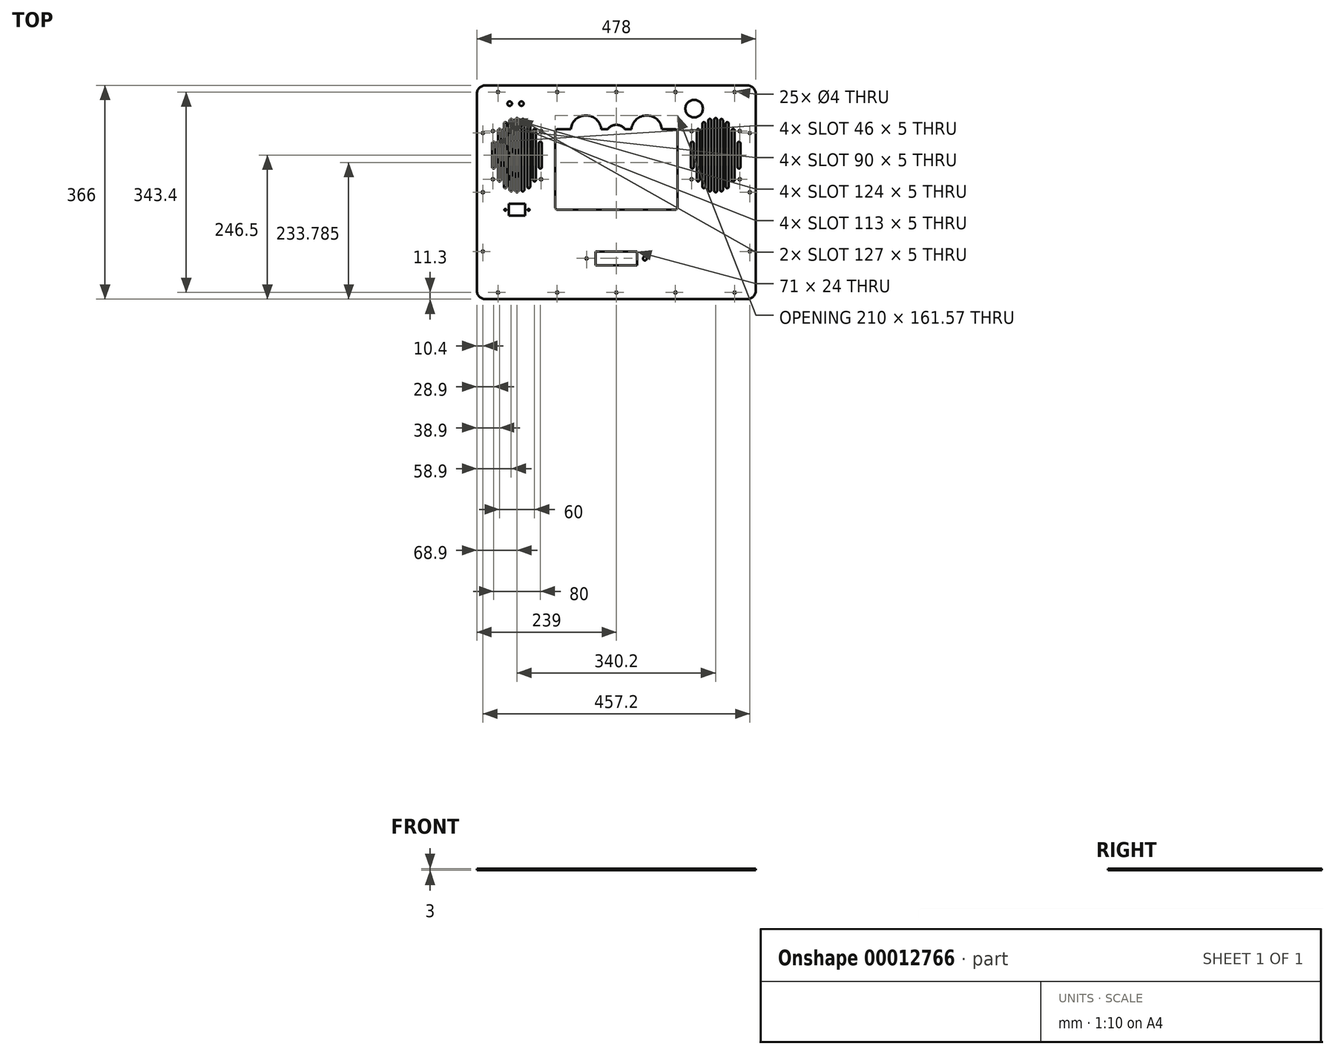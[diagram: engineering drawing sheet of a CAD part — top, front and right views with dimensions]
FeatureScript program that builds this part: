
annotation { "Feature Type Name" : "Feature", "Feature Type Description" : "" }
export const myFeature = defineFeature(function(context is Context, id is Id, definition is map)
    precondition{}
    {
        {
            var Q0;
            Q0=qCreatedBy(makeId("Top.planeOp"),FACE);
            var sketch = newSketch(context, id + "F0", { "sketchPlane" : qUnion([Q0])});
            skLineSegment(sketch, "E0.rect.bottom", {"start": v(-228.6, 171.7) * mm, "end": v(228.6, 171.7) * mm, "construction": true});
            skLineSegment(sketch, "E0.rect.top", {"start": v(-228.6, -171.7) * mm, "end": v(228.6, -171.7) * mm});
            skLineSegment(sketch, "E0.rect.left", {"start": v(-228.6, 171.7) * mm, "end": v(-228.6, -171.7) * mm, "construction": true});
            skLineSegment(sketch, "E0.rect.right", {"start": v(228.6, 171.7) * mm, "end": v(228.6, -171.7) * mm, "construction": true});
            skPoint(sketch, "E1", {"position": v(0, 171.7) * mm});
            skPoint(sketch, "E2", {"position": v(-228.6, 0) * mm});
            skCircle(sketch, "E3", {"center": v(0, 171.7) * mm, "radius": 2 * mm});
            skCircle(sketch, "E4", {"center": v(0, -171.7) * mm, "radius": 2 * mm});
            skCircle(sketch, "E5", {"center": v(-228.6, 0) * mm, "radius": 2 * mm});
            skLineSegment(sketch, "E6.rect.bottom", {"start": v(-239, 183) * mm, "end": v(239, 183) * mm});
            skLineSegment(sketch, "E6.rect.top", {"start": v(-239, -183) * mm, "end": v(239, -183) * mm});
            skLineSegment(sketch, "E6.rect.left", {"start": v(-239, 183) * mm, "end": v(-239, -183) * mm});
            skLineSegment(sketch, "E6.rect.right", {"start": v(239, 183) * mm, "end": v(239, -183) * mm});
            skLineSegment(sketch, "E7.rect.bottom", {"start": v(-222.5, 165) * mm, "end": v(222.5, 165) * mm, "construction": true});
            skLineSegment(sketch, "E7.rect.top", {"start": v(-222.5, -165) * mm, "end": v(222.5, -165) * mm});
            skLineSegment(sketch, "E7.rect.left", {"start": v(-222.5, 165) * mm, "end": v(-222.5, -165) * mm, "construction": true});
            skLineSegment(sketch, "E7.rect.right", {"start": v(222.5, 165) * mm, "end": v(222.5, -165) * mm, "construction": true});
            skCircle(sketch, "E8", {"center": v(228.6, 0) * mm, "radius": 2 * mm});
            skLineSegment(sketch, "E9.bottom", {"start": v(-192.6, 120) * mm, "end": v(-187.6, 120) * mm});
            skLineSegment(sketch, "E9.top", {"start": v(-192.6, 7) * mm, "end": v(-187.6, 7) * mm});
            skLineSegment(sketch, "E9.left", {"start": v(-192.6, 120) * mm, "end": v(-192.6, 7) * mm});
            skLineSegment(sketch, "E9.right", {"start": v(-187.6, 120) * mm, "end": v(-187.6, 7) * mm});
            skLineSegment(sketch, "E10.bottom", {"start": v(-105, 108) * mm, "end": v(105, 108) * mm});
            skLineSegment(sketch, "E10.left", {"start": v(-105, 108) * mm, "end": v(-105, -30) * mm});
            skLineSegment(sketch, "E10.right", {"start": v(105, 108) * mm, "end": v(105, -30) * mm});
            skCircle(sketch, "E11", {"center": v(-228.6, -101.3) * mm, "radius": 2 * mm});
            skLineSegment(sketch, "E12.0", {"start": v(-228.6, -171.7) * mm, "end": v(228.6, -171.7) * mm, "construction": true});
            skLineSegment(sketch, "E13", {"start": v(-228.6, 0) * mm, "end": v(228.6, 0) * mm, "construction": true});
            skLineSegment(sketch, "E14.0", {"start": v(-228.6, -101.3) * mm, "end": v(228.6, -101.3) * mm});
            skCircle(sketch, "E15", {"center": v(228.6, -101.3) * mm, "radius": 2 * mm});
            skLineSegment(sketch, "E16.0", {"start": v(-228.6, 101.3) * mm, "end": v(228.6, 101.3) * mm, "construction": true});
            skCircle(sketch, "E17", {"center": v(228.6, 101.3) * mm, "radius": 2 * mm});
            skCircle(sketch, "E18", {"center": v(-228.6, 101.3) * mm, "radius": 2 * mm});
            skLineSegment(sketch, "E19", {"start": v(0, 171.7) * mm, "end": v(0, -171.7) * mm, "construction": true});
            skLineSegment(sketch, "E20.0", {"start": v(-101.3, 171.7) * mm, "end": v(-101.3, -171.7) * mm, "construction": true});
            skCircle(sketch, "E21", {"center": v(-101.3, -171.7) * mm, "radius": 2 * mm});
            skCircle(sketch, "E22", {"center": v(-101.3, 171.7) * mm, "radius": 2 * mm});
            skLineSegment(sketch, "E23.0", {"start": v(-202.6, 171.7) * mm, "end": v(-202.6, -171.7) * mm, "construction": true});
            skCircle(sketch, "E24", {"center": v(-202.6, -171.7) * mm, "radius": 2 * mm});
            skCircle(sketch, "E25", {"center": v(-202.6, 171.7) * mm, "radius": 2 * mm});
            skLineSegment(sketch, "E26.0", {"start": v(101.3, 171.7) * mm, "end": v(101.3, -171.7) * mm, "construction": true});
            skLineSegment(sketch, "E27.0", {"start": v(202.6, 171.7) * mm, "end": v(202.6, -171.7) * mm, "construction": true});
            skCircle(sketch, "E28", {"center": v(101.3, -171.7) * mm, "radius": 2 * mm});
            skCircle(sketch, "E29", {"center": v(202.6, -171.7) * mm, "radius": 2 * mm});
            skCircle(sketch, "E30", {"center": v(101.3, 171.7) * mm, "radius": 2 * mm});
            skCircle(sketch, "E31", {"center": v(202.6, 171.7) * mm, "radius": 2 * mm});
            skPoint(sketch, "E32", {"position": v(-192.6, 63.5) * mm});
            skPoint(sketch, "E33", {"position": v(-190.28, 120) * mm});
            skLineSegment(sketch, "E34", {"start": v(-187.6, 63.5) * mm, "end": v(-192.6, 63.5) * mm, "construction": true});
            skPoint(sketch, "E35", {"position": v(-190.1, 63.5) * mm});
            skLineSegment(sketch, "E36.bottom", {"start": v(-212.6, 86.5) * mm, "end": v(-207.6, 86.5) * mm});
            skLineSegment(sketch, "E36.top", {"start": v(-212.6, 40.5) * mm, "end": v(-207.6, 40.5) * mm});
            skLineSegment(sketch, "E36.left", {"start": v(-212.6, 86.5) * mm, "end": v(-212.6, 40.5) * mm});
            skLineSegment(sketch, "E36.right", {"start": v(-207.6, 86.5) * mm, "end": v(-207.6, 40.5) * mm});
            skPoint(sketch, "E37", {"position": v(-212.6, 63.5) * mm});
            skLineSegment(sketch, "E38.bottom", {"start": v(-202.6, 108.5) * mm, "end": v(-197.6, 108.5) * mm});
            skLineSegment(sketch, "E38.top", {"start": v(-202.6, 18.5) * mm, "end": v(-197.6, 18.5) * mm});
            skLineSegment(sketch, "E38.left", {"start": v(-202.6, 108.5) * mm, "end": v(-202.6, 18.5) * mm});
            skLineSegment(sketch, "E38.right", {"start": v(-197.6, 108.5) * mm, "end": v(-197.6, 18.5) * mm});
            skPoint(sketch, "E39", {"position": v(-202.6, 63.5) * mm});
            skLineSegment(sketch, "E40.0", {"start": v(-212.6, 171.7) * mm, "end": v(-212.6, -171.7) * mm, "construction": true});
            skLineSegment(sketch, "E41.0", {"start": v(-192.6, 171.7) * mm, "end": v(-192.6, -171.7) * mm, "construction": true});
            skLineSegment(sketch, "E42.bottom", {"start": v(-182.6, 125.5) * mm, "end": v(-177.6, 125.5) * mm});
            skLineSegment(sketch, "E42.top", {"start": v(-182.6, 1.5) * mm, "end": v(-177.6, 1.5) * mm});
            skLineSegment(sketch, "E42.left", {"start": v(-182.6, 125.5) * mm, "end": v(-182.6, 1.5) * mm});
            skLineSegment(sketch, "E42.right", {"start": v(-177.6, 125.5) * mm, "end": v(-177.6, 1.5) * mm});
            skLineSegment(sketch, "E43.0", {"start": v(-182.6, 171.7) * mm, "end": v(-182.6, -171.7) * mm, "construction": true});
            skPoint(sketch, "E44", {"position": v(-182.6, 63.5) * mm});
            skLineSegment(sketch, "E45.bottom", {"start": v(-172.6, 127) * mm, "end": v(-167.6, 127) * mm});
            skLineSegment(sketch, "E45.top", {"start": v(-172.6, 0) * mm, "end": v(-167.6, 0) * mm});
            skLineSegment(sketch, "E45.left", {"start": v(-172.6, 127) * mm, "end": v(-172.6, 0) * mm});
            skLineSegment(sketch, "E45.right", {"start": v(-167.6, 127) * mm, "end": v(-167.6, 0) * mm});
            skPoint(sketch, "E46", {"position": v(-172.6, 63.5) * mm});
            skLineSegment(sketch, "E47.0", {"start": v(-172.6, 171.7) * mm, "end": v(-172.6, -171.7) * mm, "construction": true});
            skLineSegment(sketch, "E48.bottom", {"start": v(-162.6, 125.5) * mm, "end": v(-157.6, 125.5) * mm});
            skLineSegment(sketch, "E48.top", {"start": v(-162.6, 1.5) * mm, "end": v(-157.6, 1.5) * mm});
            skLineSegment(sketch, "E48.left", {"start": v(-162.6, 125.5) * mm, "end": v(-162.6, 1.5) * mm});
            skLineSegment(sketch, "E48.right", {"start": v(-157.6, 125.5) * mm, "end": v(-157.6, 1.5) * mm});
            skPoint(sketch, "E49", {"position": v(-162.6, 63.5) * mm});
            skLineSegment(sketch, "E50.0", {"start": v(-162.6, 171.7) * mm, "end": v(-162.6, -171.7) * mm, "construction": true});
            skLineSegment(sketch, "E51.bottom", {"start": v(-152.6, 120) * mm, "end": v(-147.6, 120) * mm});
            skLineSegment(sketch, "E51.top", {"start": v(-152.6, 7) * mm, "end": v(-147.6, 7) * mm});
            skLineSegment(sketch, "E51.left", {"start": v(-152.6, 120) * mm, "end": v(-152.6, 7) * mm});
            skLineSegment(sketch, "E51.right", {"start": v(-147.6, 120) * mm, "end": v(-147.6, 7) * mm});
            skPoint(sketch, "E52", {"position": v(-152.6, 63.5) * mm});
            skLineSegment(sketch, "E53.bottom", {"start": v(-142.6, 108.5) * mm, "end": v(-137.6, 108.5) * mm});
            skLineSegment(sketch, "E53.top", {"start": v(-142.6, 18.5) * mm, "end": v(-137.6, 18.5) * mm});
            skLineSegment(sketch, "E53.left", {"start": v(-142.6, 108.5) * mm, "end": v(-142.6, 18.5) * mm});
            skLineSegment(sketch, "E53.right", {"start": v(-137.6, 108.5) * mm, "end": v(-137.6, 18.5) * mm});
            skPoint(sketch, "E54", {"position": v(-142.6, 63.5) * mm});
            skLineSegment(sketch, "E55.0", {"start": v(-152.6, 171.7) * mm, "end": v(-152.6, -171.7) * mm, "construction": true});
            skLineSegment(sketch, "E56.0", {"start": v(-142.6, 171.7) * mm, "end": v(-142.6, -171.7) * mm, "construction": true});
            skLineSegment(sketch, "E57.bottom", {"start": v(-132.6, 86.5) * mm, "end": v(-127.6, 86.5) * mm});
            skLineSegment(sketch, "E57.top", {"start": v(-132.6, 40.5) * mm, "end": v(-127.6, 40.5) * mm});
            skLineSegment(sketch, "E57.left", {"start": v(-132.6, 86.5) * mm, "end": v(-132.6, 40.5) * mm});
            skLineSegment(sketch, "E57.right", {"start": v(-127.6, 86.5) * mm, "end": v(-127.6, 40.5) * mm});
            skPoint(sketch, "E58", {"position": v(-132.6, 63.5) * mm});
            skLineSegment(sketch, "E59.0", {"start": v(-132.6, 171.7) * mm, "end": v(-132.6, -171.7) * mm, "construction": true});
            skLineSegment(sketch, "E60", {"start": v(-172.6, 63.5) * mm, "end": v(-167.6, 63.5) * mm});
            skPoint(sketch, "E61", {"position": v(-170.1, 63.5) * mm});
            skLineSegment(sketch, "E62.rect.bottom", {"start": v(-128.85, 104.75) * mm, "end": v(-211.35, 104.75) * mm, "construction": true});
            skLineSegment(sketch, "E62.rect.top", {"start": v(-128.85, 22.25) * mm, "end": v(-211.35, 22.25) * mm, "construction": true});
            skLineSegment(sketch, "E62.rect.left", {"start": v(-128.85, 104.75) * mm, "end": v(-128.85, 22.25) * mm, "construction": true});
            skLineSegment(sketch, "E62.rect.right", {"start": v(-211.35, 104.75) * mm, "end": v(-211.35, 22.25) * mm, "construction": true});
            skCircle(sketch, "E63", {"center": v(-128.85, 104.75) * mm, "radius": 2 * mm});
            skCircle(sketch, "E64", {"center": v(-128.85, 22.25) * mm, "radius": 2 * mm});
            skCircle(sketch, "E65", {"center": v(-211.35, 22.25) * mm, "radius": 2 * mm});
            skCircle(sketch, "E66", {"center": v(-211.35, 104.75) * mm, "radius": 2 * mm});
            skLineSegment(sketch, "E67.0.MirrorCS", {"start": v(192.6, 120) * mm, "end": v(187.6, 120) * mm});
            skLineSegment(sketch, "E67.1.MirrorCS", {"start": v(152.6, 7) * mm, "end": v(147.6, 7) * mm});
            skLineSegment(sketch, "E67.2.MirrorCS", {"start": v(182.6, 125.5) * mm, "end": v(177.6, 125.5) * mm});
            skLineSegment(sketch, "E67.3.MirrorCS", {"start": v(192.6, 7) * mm, "end": v(187.6, 7) * mm});
            skLineSegment(sketch, "E67.4.MirrorCS", {"start": v(152.6, 120) * mm, "end": v(147.6, 120) * mm});
            skLineSegment(sketch, "E67.5.MirrorCS", {"start": v(162.6, 1.5) * mm, "end": v(157.6, 1.5) * mm});
            skLineSegment(sketch, "E67.6.MirrorCS", {"start": v(132.6, 86.5) * mm, "end": v(127.6, 86.5) * mm});
            skLineSegment(sketch, "E67.7.MirrorCS", {"start": v(202.6, 108.5) * mm, "end": v(197.6, 108.5) * mm});
            skLineSegment(sketch, "E67.8.MirrorCS", {"start": v(172.6, 63.5) * mm, "end": v(167.6, 63.5) * mm});
            skLineSegment(sketch, "E67.9.MirrorCS", {"start": v(172.6, 0) * mm, "end": v(167.6, 0) * mm});
            skLineSegment(sketch, "E67.10.MirrorCS", {"start": v(212.6, 40.5) * mm, "end": v(207.6, 40.5) * mm});
            skLineSegment(sketch, "E67.11.MirrorCS", {"start": v(142.6, 108.5) * mm, "end": v(137.6, 108.5) * mm});
            skCircle(sketch, "E67.12.MirrorC", {"center": v(211.35, 22.25) * mm, "radius": 2 * mm});
            skLineSegment(sketch, "E67.13.MirrorCS", {"start": v(172.6, 127) * mm, "end": v(167.6, 127) * mm});
            skLineSegment(sketch, "E67.14.MirrorCS", {"start": v(212.6, 86.5) * mm, "end": v(207.6, 86.5) * mm});
            skCircle(sketch, "E67.15.MirrorC", {"center": v(128.85, 104.75) * mm, "radius": 2 * mm});
            skCircle(sketch, "E67.16.MirrorC", {"center": v(128.85, 22.25) * mm, "radius": 2 * mm});
            skLineSegment(sketch, "E67.17.MirrorCS", {"start": v(182.6, 1.5) * mm, "end": v(177.6, 1.5) * mm});
            skLineSegment(sketch, "E67.18.MirrorCS", {"start": v(202.6, 18.5) * mm, "end": v(197.6, 18.5) * mm});
            skLineSegment(sketch, "E67.19.MirrorCS", {"start": v(132.6, 40.5) * mm, "end": v(127.6, 40.5) * mm});
            skLineSegment(sketch, "E67.20.MirrorCS", {"start": v(162.6, 125.5) * mm, "end": v(157.6, 125.5) * mm});
            skCircle(sketch, "E67.21.MirrorC", {"center": v(211.35, 104.75) * mm, "radius": 2 * mm});
            skLineSegment(sketch, "E67.22.MirrorCS", {"start": v(187.6, 63.5) * mm, "end": v(192.6, 63.5) * mm, "construction": true});
            skPoint(sketch, "E67.23.MirrorP", {"position": v(170.1, 63.5) * mm});
            skPoint(sketch, "E67.24.MirrorP", {"position": v(172.6, 63.5) * mm});
            skLineSegment(sketch, "E67.25.MirrorCS", {"start": v(142.6, 18.5) * mm, "end": v(137.6, 18.5) * mm});
            skLineSegment(sketch, "E67.26.MirrorCS", {"start": v(172.6, 127) * mm, "end": v(172.6, 0) * mm});
            skLineSegment(sketch, "E67.27.MirrorCS", {"start": v(212.6, 86.5) * mm, "end": v(212.6, 40.5) * mm});
            skPoint(sketch, "E67.28.MirrorP", {"position": v(190.1, 63.5) * mm});
            skLineSegment(sketch, "E67.29.MirrorCS", {"start": v(128.85, 22.25) * mm, "end": v(211.35, 22.25) * mm, "construction": true});
            skPoint(sketch, "E67.30.MirrorP", {"position": v(212.6, 63.5) * mm});
            skLineSegment(sketch, "E67.31.MirrorCS", {"start": v(207.6, 86.5) * mm, "end": v(207.6, 40.5) * mm});
            skLineSegment(sketch, "E67.32.MirrorCS", {"start": v(167.6, 127) * mm, "end": v(167.6, 0) * mm});
            skPoint(sketch, "E67.33.MirrorP", {"position": v(202.6, 63.5) * mm});
            skLineSegment(sketch, "E67.34.MirrorCS", {"start": v(128.85, 104.75) * mm, "end": v(211.35, 104.75) * mm, "construction": true});
            skPoint(sketch, "E67.35.MirrorP", {"position": v(132.6, 63.5) * mm});
            skLineSegment(sketch, "E67.36.MirrorCS", {"start": v(202.6, 108.5) * mm, "end": v(202.6, 18.5) * mm});
            skLineSegment(sketch, "E67.37.MirrorCS", {"start": v(132.6, 86.5) * mm, "end": v(132.6, 40.5) * mm});
            skLineSegment(sketch, "E67.38.MirrorCS", {"start": v(192.6, 120) * mm, "end": v(192.6, 7) * mm});
            skPoint(sketch, "E67.39.MirrorP", {"position": v(162.6, 63.5) * mm});
            skLineSegment(sketch, "E67.40.MirrorCS", {"start": v(162.6, 125.5) * mm, "end": v(162.6, 1.5) * mm});
            skLineSegment(sketch, "E67.41.MirrorCS", {"start": v(127.6, 86.5) * mm, "end": v(127.6, 40.5) * mm});
            skLineSegment(sketch, "E67.42.MirrorCS", {"start": v(137.6, 108.5) * mm, "end": v(137.6, 18.5) * mm});
            skLineSegment(sketch, "E67.43.MirrorCS", {"start": v(197.6, 108.5) * mm, "end": v(197.6, 18.5) * mm});
            skPoint(sketch, "E67.44.MirrorP", {"position": v(142.6, 63.5) * mm});
            skLineSegment(sketch, "E67.45.MirrorCS", {"start": v(177.6, 125.5) * mm, "end": v(177.6, 1.5) * mm});
            skPoint(sketch, "E67.46.MirrorP", {"position": v(190.28, 120) * mm});
            skPoint(sketch, "E67.47.MirrorP", {"position": v(152.6, 63.5) * mm});
            skLineSegment(sketch, "E67.48.MirrorCS", {"start": v(142.6, 108.5) * mm, "end": v(142.6, 18.5) * mm});
            skPoint(sketch, "E67.49.MirrorP", {"position": v(192.6, 63.5) * mm});
            skPoint(sketch, "E67.50.MirrorP", {"position": v(170.1, 63.5) * mm});
            skLineSegment(sketch, "E67.51.MirrorCS", {"start": v(157.6, 125.5) * mm, "end": v(157.6, 1.5) * mm});
            skPoint(sketch, "E67.52.MirrorP", {"position": v(182.6, 63.5) * mm});
            skLineSegment(sketch, "E67.53.MirrorCS", {"start": v(128.85, 104.75) * mm, "end": v(128.85, 22.25) * mm, "construction": true});
            skLineSegment(sketch, "E67.54.MirrorCS", {"start": v(152.6, 120) * mm, "end": v(152.6, 7) * mm});
            skLineSegment(sketch, "E67.55.MirrorCS", {"start": v(187.6, 120) * mm, "end": v(187.6, 7) * mm});
            skLineSegment(sketch, "E67.56.MirrorCS", {"start": v(211.35, 104.75) * mm, "end": v(211.35, 22.25) * mm, "construction": true});
            skLineSegment(sketch, "E67.57.MirrorCS", {"start": v(147.6, 120) * mm, "end": v(147.6, 7) * mm});
            skLineSegment(sketch, "E67.58.MirrorCS", {"start": v(182.6, 125.5) * mm, "end": v(182.6, 1.5) * mm});
            skCircle(sketch, "E68", {"center": v(133.3, 143.2) * mm, "radius": 15 * mm});
            skLineSegment(sketch, "E69.bottom", {"start": v(-35.5, -101.3) * mm, "end": v(35.5, -101.3) * mm});
            skLineSegment(sketch, "E69.top", {"start": v(-35.5, -125.3) * mm, "end": v(35.5, -125.3) * mm});
            skLineSegment(sketch, "E69.left", {"start": v(-35.5, -101.3) * mm, "end": v(-35.5, -125.3) * mm});
            skLineSegment(sketch, "E69.right", {"start": v(35.5, -101.3) * mm, "end": v(35.5, -125.3) * mm});
            skPoint(sketch, "E70", {"position": v(0, -125.3) * mm});
            skPoint(sketch, "E71", {"position": v(-412.87, -32.62) * mm});
            skLineSegment(sketch, "E72", {"start": v(0, -125.3) * mm, "end": v(0, -101.3) * mm, "construction": true});
            skPoint(sketch, "E73", {"position": v(-35.5, -113.3) * mm});
            skLineSegment(sketch, "E74.0", {"start": v(-51, -101.3) * mm, "end": v(-51, -125.3) * mm, "construction": true});
            skPoint(sketch, "E75", {"position": v(-51, -113.3) * mm});
            skPoint(sketch, "E76", {"position": v(35.5, -113.3) * mm});
            skLineSegment(sketch, "E77.0", {"start": v(48.9, -101.3) * mm, "end": v(48.9, -125.3) * mm, "construction": true});
            skPoint(sketch, "E78", {"position": v(48.9, -113.3) * mm});
            skCircle(sketch, "E79", {"center": v(48.9, -113.3) * mm, "radius": 3.4 * mm});
            skLineSegment(sketch, "E80.0", {"start": v(-228.6, 151.7) * mm, "end": v(228.6, 151.7) * mm, "construction": true});
            skCircle(sketch, "E81", {"center": v(-182.6, 151.7) * mm, "radius": 3.9 * mm});
            skCircle(sketch, "E82", {"center": v(-162.6, 151.7) * mm, "radius": 3.9 * mm});
            skCircle(sketch, "E83", {"center": v(-51, -113.3) * mm, "radius": 2 * mm});
            skLineSegment(sketch, "E84.0", {"start": v(-228.6, 63.7) * mm, "end": v(228.6, 63.7) * mm, "construction": true});
            skLineSegment(sketch, "E85.0", {"start": v(-228.6, 143.2) * mm, "end": v(228.6, 143.2) * mm, "construction": true});
            skLineSegment(sketch, "E86.0", {"start": v(133.3, 171.7) * mm, "end": v(133.3, -171.7) * mm, "construction": true});
            skCircle(sketch, "E87", {"center": v(-190.1, -29.96) * mm, "radius": 1.6 * mm});
            skLineSegment(sketch, "E88.rect.bottom", {"start": v(-184.1, -19.96) * mm, "end": v(-156.1, -19.96) * mm});
            skLineSegment(sketch, "E88.rect.top", {"start": v(-184.1, -39.96) * mm, "end": v(-156.1, -39.96) * mm});
            skLineSegment(sketch, "E88.rect.left", {"start": v(-184.1, -19.96) * mm, "end": v(-184.1, -39.96) * mm});
            skLineSegment(sketch, "E88.rect.right", {"start": v(-156.1, -19.96) * mm, "end": v(-156.1, -39.96) * mm});
            skPoint(sketch, "E88.rect.middle", {"position": v(-170.1, -29.96) * mm});
            skLineSegment(sketch, "E89", {"start": v(-170.1, -29.96) * mm, "end": v(-190.1, -29.96) * mm, "construction": true});
            skLineSegment(sketch, "E90", {"start": v(-170.1, -29.96) * mm, "end": v(-150.1, -29.96) * mm, "construction": true});
            skLineSegment(sketch, "E91.0", {"start": v(-228.6, -30) * mm, "end": v(228.6, -30) * mm, "construction": true});
            skCircle(sketch, "E92", {"center": v(-150.1, -29.96) * mm, "radius": 1.6 * mm});
            skLineSegment(sketch, "E93", {"start": v(-105, -30) * mm, "end": v(105, -30) * mm});
            skLineSegment(sketch, "E94", {"start": v(-105, 105.37) * mm, "end": v(105, 105.37) * mm, "construction": true});
            skCircle(sketch, "E95", {"center": v(-52, 105.37) * mm, "radius": 26.2 * mm});
            skCircle(sketch, "E96.MirrorC", {"center": v(52, 105.37) * mm, "radius": 26.2 * mm});
            skLineSegment(sketch, "E97", {"start": v(-105, 97.1) * mm, "end": v(105, 97.1) * mm, "construction": true});
            skCircle(sketch, "E98", {"center": v(0, 97.1) * mm, "radius": 18.4 * mm});
            skSolve(sketch);
        }
        {
            var Q0;
            Q0=makeQuery(id+"F0.imprint","IMPRINT",FACE,{"disambiguationData":[TD([[makeQuery(id+"F0.imprint","IMPRINT",EDGE,{"derivedFrom":sQuery(id+"F0.wireOp",EDGE,"E3")}),-1.0]])]});
            extrude(context, id + "F1", {"entities" : qUnion([Q0]), "depth" : 3 * mm});
        }
        {
            var Q0;
            Q0=makeQuery(id+"F1.opExtrude","SWEPT_EDGE",EDGE,{"disambiguationData":[OSD([sQuery(id+"F0.wireOp",EDGE,"E36.bottom"),sQuery(id+"F0.wireOp",EDGE,"E36.left")])]});
            var Q1;
            Q1=makeQuery(id+"F1.opExtrude","SWEPT_EDGE",EDGE,{"disambiguationData":[OSD([sQuery(id+"F0.wireOp",EDGE,"E38.bottom"),sQuery(id+"F0.wireOp",EDGE,"E38.left")])]});
            var Q2;
            Q2=makeQuery(id+"F1.opExtrude","SWEPT_EDGE",EDGE,{"disambiguationData":[OSD([sQuery(id+"F0.wireOp",EDGE,"E9.bottom"),sQuery(id+"F0.wireOp",EDGE,"E9.left")])]});
            var Q3;
            Q3=makeQuery(id+"F1.opExtrude","SWEPT_EDGE",EDGE,{"disambiguationData":[OSD([sQuery(id+"F0.wireOp",EDGE,"E42.bottom"),sQuery(id+"F0.wireOp",EDGE,"E42.left")])]});
            var Q4;
            Q4=makeQuery(id+"F1.opExtrude","SWEPT_EDGE",EDGE,{"disambiguationData":[OSD([sQuery(id+"F0.wireOp",EDGE,"E45.bottom"),sQuery(id+"F0.wireOp",EDGE,"E45.left")])]});
            var Q5;
            Q5=makeQuery(id+"F1.opExtrude","SWEPT_EDGE",EDGE,{"disambiguationData":[OSD([sQuery(id+"F0.wireOp",EDGE,"E48.bottom"),sQuery(id+"F0.wireOp",EDGE,"E48.left")])]});
            var Q6;
            Q6=makeQuery(id+"F1.opExtrude","SWEPT_EDGE",EDGE,{"disambiguationData":[OSD([sQuery(id+"F0.wireOp",EDGE,"E51.bottom"),sQuery(id+"F0.wireOp",EDGE,"E51.left")])]});
            var Q7;
            Q7=makeQuery(id+"F1.opExtrude","SWEPT_EDGE",EDGE,{"disambiguationData":[OSD([sQuery(id+"F0.wireOp",EDGE,"E53.bottom"),sQuery(id+"F0.wireOp",EDGE,"E53.left")])]});
            var Q8;
            Q8=makeQuery(id+"F1.opExtrude","SWEPT_EDGE",EDGE,{"disambiguationData":[OSD([sQuery(id+"F0.wireOp",EDGE,"E57.bottom"),sQuery(id+"F0.wireOp",EDGE,"E57.left")])]});
            var Q9;
            Q9=makeQuery(id+"F1.opExtrude","SWEPT_EDGE",EDGE,{"disambiguationData":[OSD([sQuery(id+"F0.wireOp",EDGE,"E57.bottom"),sQuery(id+"F0.wireOp",EDGE,"E57.right")])]});
            var Q10;
            Q10=makeQuery(id+"F1.opExtrude","SWEPT_EDGE",EDGE,{"disambiguationData":[OSD([sQuery(id+"F0.wireOp",EDGE,"E53.bottom"),sQuery(id+"F0.wireOp",EDGE,"E53.right")])]});
            var Q11;
            Q11=makeQuery(id+"F1.opExtrude","SWEPT_EDGE",EDGE,{"disambiguationData":[OSD([sQuery(id+"F0.wireOp",EDGE,"E51.bottom"),sQuery(id+"F0.wireOp",EDGE,"E51.right")])]});
            var Q12;
            Q12=makeQuery(id+"F1.opExtrude","SWEPT_EDGE",EDGE,{"disambiguationData":[OSD([sQuery(id+"F0.wireOp",EDGE,"E48.bottom"),sQuery(id+"F0.wireOp",EDGE,"E48.right")])]});
            var Q13;
            Q13=makeQuery(id+"F1.opExtrude","SWEPT_EDGE",EDGE,{"disambiguationData":[OSD([sQuery(id+"F0.wireOp",EDGE,"E45.bottom"),sQuery(id+"F0.wireOp",EDGE,"E45.right")])]});
            var Q14;
            Q14=makeQuery(id+"F1.opExtrude","SWEPT_EDGE",EDGE,{"disambiguationData":[OSD([sQuery(id+"F0.wireOp",EDGE,"E42.bottom"),sQuery(id+"F0.wireOp",EDGE,"E42.right")])]});
            var Q15;
            Q15=makeQuery(id+"F1.opExtrude","SWEPT_EDGE",EDGE,{"disambiguationData":[OSD([sQuery(id+"F0.wireOp",EDGE,"E9.bottom"),sQuery(id+"F0.wireOp",EDGE,"E9.right")])]});
            var Q16;
            Q16=makeQuery(id+"F1.opExtrude","SWEPT_EDGE",EDGE,{"disambiguationData":[OSD([sQuery(id+"F0.wireOp",EDGE,"E38.bottom"),sQuery(id+"F0.wireOp",EDGE,"E38.right")])]});
            var Q17;
            Q17=makeQuery(id+"F1.opExtrude","SWEPT_EDGE",EDGE,{"disambiguationData":[OSD([sQuery(id+"F0.wireOp",EDGE,"E36.bottom"),sQuery(id+"F0.wireOp",EDGE,"E36.right")])]});
            var Q18;
            Q18=makeQuery(id+"F1.opExtrude","SWEPT_EDGE",EDGE,{"disambiguationData":[OSD([sQuery(id+"F0.wireOp",EDGE,"E36.top"),sQuery(id+"F0.wireOp",EDGE,"E36.left")])]});
            var Q19;
            Q19=makeQuery(id+"F1.opExtrude","SWEPT_EDGE",EDGE,{"disambiguationData":[OSD([sQuery(id+"F0.wireOp",EDGE,"E38.top"),sQuery(id+"F0.wireOp",EDGE,"E38.left")])]});
            var Q20;
            Q20=makeQuery(id+"F1.opExtrude","SWEPT_EDGE",EDGE,{"disambiguationData":[OSD([sQuery(id+"F0.wireOp",EDGE,"E9.top"),sQuery(id+"F0.wireOp",EDGE,"E9.left")])]});
            var Q21;
            Q21=makeQuery(id+"F1.opExtrude","SWEPT_EDGE",EDGE,{"disambiguationData":[OSD([sQuery(id+"F0.wireOp",EDGE,"E42.top"),sQuery(id+"F0.wireOp",EDGE,"E42.left")])]});
            var Q22;
            Q22=makeQuery(id+"F1.opExtrude","SWEPT_EDGE",EDGE,{"disambiguationData":[OSD([sQuery(id+"F0.wireOp",EDGE,"E45.top"),sQuery(id+"F0.wireOp",EDGE,"E45.left")])]});
            var Q23;
            Q23=makeQuery(id+"F1.opExtrude","SWEPT_EDGE",EDGE,{"disambiguationData":[OSD([sQuery(id+"F0.wireOp",EDGE,"E48.top"),sQuery(id+"F0.wireOp",EDGE,"E48.left")])]});
            var Q24;
            Q24=makeQuery(id+"F1.opExtrude","SWEPT_EDGE",EDGE,{"disambiguationData":[OSD([sQuery(id+"F0.wireOp",EDGE,"E51.top"),sQuery(id+"F0.wireOp",EDGE,"E51.left")])]});
            var Q25;
            Q25=makeQuery(id+"F1.opExtrude","SWEPT_EDGE",EDGE,{"disambiguationData":[OSD([sQuery(id+"F0.wireOp",EDGE,"E53.top"),sQuery(id+"F0.wireOp",EDGE,"E53.left")])]});
            var Q26;
            Q26=makeQuery(id+"F1.opExtrude","SWEPT_EDGE",EDGE,{"disambiguationData":[OSD([sQuery(id+"F0.wireOp",EDGE,"E57.top"),sQuery(id+"F0.wireOp",EDGE,"E57.left")])]});
            var Q27;
            Q27=makeQuery(id+"F1.opExtrude","SWEPT_EDGE",EDGE,{"disambiguationData":[OSD([sQuery(id+"F0.wireOp",EDGE,"E57.top"),sQuery(id+"F0.wireOp",EDGE,"E57.right")])]});
            var Q28;
            Q28=makeQuery(id+"F1.opExtrude","SWEPT_EDGE",EDGE,{"disambiguationData":[OSD([sQuery(id+"F0.wireOp",EDGE,"E53.top"),sQuery(id+"F0.wireOp",EDGE,"E53.right")])]});
            var Q29;
            Q29=makeQuery(id+"F1.opExtrude","SWEPT_EDGE",EDGE,{"disambiguationData":[OSD([sQuery(id+"F0.wireOp",EDGE,"E51.top"),sQuery(id+"F0.wireOp",EDGE,"E51.right")])]});
            var Q30;
            Q30=makeQuery(id+"F1.opExtrude","SWEPT_EDGE",EDGE,{"disambiguationData":[OSD([sQuery(id+"F0.wireOp",EDGE,"E48.top"),sQuery(id+"F0.wireOp",EDGE,"E48.right")])]});
            var Q31;
            Q31=makeQuery(id+"F1.opExtrude","SWEPT_EDGE",EDGE,{"disambiguationData":[OSD([sQuery(id+"F0.wireOp",EDGE,"E45.top"),sQuery(id+"F0.wireOp",EDGE,"E45.right")])]});
            var Q32;
            Q32=makeQuery(id+"F1.opExtrude","SWEPT_EDGE",EDGE,{"disambiguationData":[OSD([sQuery(id+"F0.wireOp",EDGE,"E42.top"),sQuery(id+"F0.wireOp",EDGE,"E42.right")])]});
            var Q33;
            Q33=makeQuery(id+"F1.opExtrude","SWEPT_EDGE",EDGE,{"disambiguationData":[OSD([sQuery(id+"F0.wireOp",EDGE,"E9.top"),sQuery(id+"F0.wireOp",EDGE,"E9.right")])]});
            var Q34;
            Q34=makeQuery(id+"F1.opExtrude","SWEPT_EDGE",EDGE,{"disambiguationData":[OSD([sQuery(id+"F0.wireOp",EDGE,"E38.top"),sQuery(id+"F0.wireOp",EDGE,"E38.right")])]});
            var Q35;
            Q35=makeQuery(id+"F1.opExtrude","SWEPT_EDGE",EDGE,{"disambiguationData":[OSD([sQuery(id+"F0.wireOp",EDGE,"E36.top"),sQuery(id+"F0.wireOp",EDGE,"E36.right")])]});
            fillet(context, id + "F2", {"entities" : qUnion([Q0, Q1, Q2, Q3, Q4, Q5, Q6, Q7, Q8, Q9, Q10, Q11, Q12, Q13, Q14, Q15, Q16, Q17, Q18, Q19, Q20, Q21, Q22, Q23, Q24, Q25, Q26, Q27, Q28, Q29, Q30, Q31, Q32, Q33, Q34, Q35]), "radius" : 2.5 * mm, "tangentPropagation" : true, "allowEdgeOverflow" : false});
        }
        {
            var Q0;
            Q0=makeQuery(id+"F1.opExtrude","SWEPT_EDGE",EDGE,{"disambiguationData":[OSD([sQuery(id+"F0.wireOp",EDGE,"E67.6.MirrorCS"),sQuery(id+"F0.wireOp",EDGE,"E67.41.MirrorCS")])]});
            var Q1;
            Q1=makeQuery(id+"F1.opExtrude","SWEPT_EDGE",EDGE,{"disambiguationData":[OSD([sQuery(id+"F0.wireOp",EDGE,"E67.11.MirrorCS"),sQuery(id+"F0.wireOp",EDGE,"E67.42.MirrorCS")])]});
            var Q2;
            Q2=makeQuery(id+"F1.opExtrude","SWEPT_EDGE",EDGE,{"disambiguationData":[OSD([sQuery(id+"F0.wireOp",EDGE,"E67.4.MirrorCS"),sQuery(id+"F0.wireOp",EDGE,"E67.57.MirrorCS")])]});
            var Q3;
            Q3=makeQuery(id+"F1.opExtrude","SWEPT_EDGE",EDGE,{"disambiguationData":[OSD([sQuery(id+"F0.wireOp",EDGE,"E67.6.MirrorCS"),sQuery(id+"F0.wireOp",EDGE,"E67.37.MirrorCS")])]});
            var Q4;
            Q4=makeQuery(id+"F1.opExtrude","SWEPT_EDGE",EDGE,{"disambiguationData":[OSD([sQuery(id+"F0.wireOp",EDGE,"E67.11.MirrorCS"),sQuery(id+"F0.wireOp",EDGE,"E67.48.MirrorCS")])]});
            var Q5;
            Q5=makeQuery(id+"F1.opExtrude","SWEPT_EDGE",EDGE,{"disambiguationData":[OSD([sQuery(id+"F0.wireOp",EDGE,"E67.4.MirrorCS"),sQuery(id+"F0.wireOp",EDGE,"E67.54.MirrorCS")])]});
            var Q6;
            Q6=makeQuery(id+"F1.opExtrude","SWEPT_EDGE",EDGE,{"disambiguationData":[OSD([sQuery(id+"F0.wireOp",EDGE,"E67.20.MirrorCS"),sQuery(id+"F0.wireOp",EDGE,"E67.40.MirrorCS")])]});
            var Q7;
            Q7=makeQuery(id+"F1.opExtrude","SWEPT_EDGE",EDGE,{"disambiguationData":[OSD([sQuery(id+"F0.wireOp",EDGE,"E67.13.MirrorCS"),sQuery(id+"F0.wireOp",EDGE,"E67.26.MirrorCS")])]});
            var Q8;
            Q8=makeQuery(id+"F1.opExtrude","SWEPT_EDGE",EDGE,{"disambiguationData":[OSD([sQuery(id+"F0.wireOp",EDGE,"E67.2.MirrorCS"),sQuery(id+"F0.wireOp",EDGE,"E67.58.MirrorCS")])]});
            var Q9;
            Q9=makeQuery(id+"F1.opExtrude","SWEPT_EDGE",EDGE,{"disambiguationData":[OSD([sQuery(id+"F0.wireOp",EDGE,"E67.0.MirrorCS"),sQuery(id+"F0.wireOp",EDGE,"E67.38.MirrorCS")])]});
            var Q10;
            Q10=makeQuery(id+"F1.opExtrude","SWEPT_EDGE",EDGE,{"disambiguationData":[OSD([sQuery(id+"F0.wireOp",EDGE,"E67.7.MirrorCS"),sQuery(id+"F0.wireOp",EDGE,"E67.36.MirrorCS")])]});
            var Q11;
            Q11=makeQuery(id+"F1.opExtrude","SWEPT_EDGE",EDGE,{"disambiguationData":[OSD([sQuery(id+"F0.wireOp",EDGE,"E67.14.MirrorCS"),sQuery(id+"F0.wireOp",EDGE,"E67.27.MirrorCS")])]});
            var Q12;
            Q12=makeQuery(id+"F1.opExtrude","SWEPT_EDGE",EDGE,{"disambiguationData":[OSD([sQuery(id+"F0.wireOp",EDGE,"E67.20.MirrorCS"),sQuery(id+"F0.wireOp",EDGE,"E67.51.MirrorCS")])]});
            var Q13;
            Q13=makeQuery(id+"F1.opExtrude","SWEPT_EDGE",EDGE,{"disambiguationData":[OSD([sQuery(id+"F0.wireOp",EDGE,"E67.13.MirrorCS"),sQuery(id+"F0.wireOp",EDGE,"E67.32.MirrorCS")])]});
            var Q14;
            Q14=makeQuery(id+"F1.opExtrude","SWEPT_EDGE",EDGE,{"disambiguationData":[OSD([sQuery(id+"F0.wireOp",EDGE,"E67.2.MirrorCS"),sQuery(id+"F0.wireOp",EDGE,"E67.45.MirrorCS")])]});
            var Q15;
            Q15=makeQuery(id+"F1.opExtrude","SWEPT_EDGE",EDGE,{"disambiguationData":[OSD([sQuery(id+"F0.wireOp",EDGE,"E67.0.MirrorCS"),sQuery(id+"F0.wireOp",EDGE,"E67.55.MirrorCS")])]});
            var Q16;
            Q16=makeQuery(id+"F1.opExtrude","SWEPT_EDGE",EDGE,{"disambiguationData":[OSD([sQuery(id+"F0.wireOp",EDGE,"E67.7.MirrorCS"),sQuery(id+"F0.wireOp",EDGE,"E67.43.MirrorCS")])]});
            var Q17;
            Q17=makeQuery(id+"F1.opExtrude","SWEPT_EDGE",EDGE,{"disambiguationData":[OSD([sQuery(id+"F0.wireOp",EDGE,"E67.14.MirrorCS"),sQuery(id+"F0.wireOp",EDGE,"E67.31.MirrorCS")])]});
            var Q18;
            Q18=makeQuery(id+"F1.opExtrude","SWEPT_EDGE",EDGE,{"disambiguationData":[OSD([sQuery(id+"F0.wireOp",EDGE,"E67.10.MirrorCS"),sQuery(id+"F0.wireOp",EDGE,"E67.27.MirrorCS")])]});
            var Q19;
            Q19=makeQuery(id+"F1.opExtrude","SWEPT_EDGE",EDGE,{"disambiguationData":[OSD([sQuery(id+"F0.wireOp",EDGE,"E67.18.MirrorCS"),sQuery(id+"F0.wireOp",EDGE,"E67.36.MirrorCS")])]});
            var Q20;
            Q20=makeQuery(id+"F1.opExtrude","SWEPT_EDGE",EDGE,{"disambiguationData":[OSD([sQuery(id+"F0.wireOp",EDGE,"E67.3.MirrorCS"),sQuery(id+"F0.wireOp",EDGE,"E67.38.MirrorCS")])]});
            var Q21;
            Q21=makeQuery(id+"F1.opExtrude","SWEPT_EDGE",EDGE,{"disambiguationData":[OSD([sQuery(id+"F0.wireOp",EDGE,"E67.17.MirrorCS"),sQuery(id+"F0.wireOp",EDGE,"E67.58.MirrorCS")])]});
            var Q22;
            Q22=makeQuery(id+"F1.opExtrude","SWEPT_EDGE",EDGE,{"disambiguationData":[OSD([sQuery(id+"F0.wireOp",EDGE,"E67.9.MirrorCS"),sQuery(id+"F0.wireOp",EDGE,"E67.26.MirrorCS")])]});
            var Q23;
            Q23=makeQuery(id+"F1.opExtrude","SWEPT_EDGE",EDGE,{"disambiguationData":[OSD([sQuery(id+"F0.wireOp",EDGE,"E67.5.MirrorCS"),sQuery(id+"F0.wireOp",EDGE,"E67.40.MirrorCS")])]});
            var Q24;
            Q24=makeQuery(id+"F1.opExtrude","SWEPT_EDGE",EDGE,{"disambiguationData":[OSD([sQuery(id+"F0.wireOp",EDGE,"E67.1.MirrorCS"),sQuery(id+"F0.wireOp",EDGE,"E67.54.MirrorCS")])]});
            var Q25;
            Q25=makeQuery(id+"F1.opExtrude","SWEPT_EDGE",EDGE,{"disambiguationData":[OSD([sQuery(id+"F0.wireOp",EDGE,"E67.25.MirrorCS"),sQuery(id+"F0.wireOp",EDGE,"E67.48.MirrorCS")])]});
            var Q26;
            Q26=makeQuery(id+"F1.opExtrude","SWEPT_EDGE",EDGE,{"disambiguationData":[OSD([sQuery(id+"F0.wireOp",EDGE,"E67.19.MirrorCS"),sQuery(id+"F0.wireOp",EDGE,"E67.37.MirrorCS")])]});
            var Q27;
            Q27=makeQuery(id+"F1.opExtrude","SWEPT_EDGE",EDGE,{"disambiguationData":[OSD([sQuery(id+"F0.wireOp",EDGE,"E67.19.MirrorCS"),sQuery(id+"F0.wireOp",EDGE,"E67.41.MirrorCS")])]});
            var Q28;
            Q28=makeQuery(id+"F1.opExtrude","SWEPT_EDGE",EDGE,{"disambiguationData":[OSD([sQuery(id+"F0.wireOp",EDGE,"E67.25.MirrorCS"),sQuery(id+"F0.wireOp",EDGE,"E67.42.MirrorCS")])]});
            var Q29;
            Q29=makeQuery(id+"F1.opExtrude","SWEPT_EDGE",EDGE,{"disambiguationData":[OSD([sQuery(id+"F0.wireOp",EDGE,"E67.1.MirrorCS"),sQuery(id+"F0.wireOp",EDGE,"E67.57.MirrorCS")])]});
            var Q30;
            Q30=makeQuery(id+"F1.opExtrude","SWEPT_EDGE",EDGE,{"disambiguationData":[OSD([sQuery(id+"F0.wireOp",EDGE,"E67.5.MirrorCS"),sQuery(id+"F0.wireOp",EDGE,"E67.51.MirrorCS")])]});
            var Q31;
            Q31=makeQuery(id+"F1.opExtrude","SWEPT_EDGE",EDGE,{"disambiguationData":[OSD([sQuery(id+"F0.wireOp",EDGE,"E67.9.MirrorCS"),sQuery(id+"F0.wireOp",EDGE,"E67.32.MirrorCS")])]});
            var Q32;
            Q32=makeQuery(id+"F1.opExtrude","SWEPT_EDGE",EDGE,{"disambiguationData":[OSD([sQuery(id+"F0.wireOp",EDGE,"E67.17.MirrorCS"),sQuery(id+"F0.wireOp",EDGE,"E67.45.MirrorCS")])]});
            var Q33;
            Q33=makeQuery(id+"F1.opExtrude","SWEPT_EDGE",EDGE,{"disambiguationData":[OSD([sQuery(id+"F0.wireOp",EDGE,"E67.3.MirrorCS"),sQuery(id+"F0.wireOp",EDGE,"E67.55.MirrorCS")])]});
            var Q34;
            Q34=makeQuery(id+"F1.opExtrude","SWEPT_EDGE",EDGE,{"disambiguationData":[OSD([sQuery(id+"F0.wireOp",EDGE,"E67.18.MirrorCS"),sQuery(id+"F0.wireOp",EDGE,"E67.43.MirrorCS")])]});
            var Q35;
            Q35=makeQuery(id+"F1.opExtrude","SWEPT_EDGE",EDGE,{"disambiguationData":[OSD([sQuery(id+"F0.wireOp",EDGE,"E67.10.MirrorCS"),sQuery(id+"F0.wireOp",EDGE,"E67.31.MirrorCS")])]});
            fillet(context, id + "F3", {"entities" : qUnion([Q0, Q1, Q2, Q3, Q4, Q5, Q6, Q7, Q8, Q9, Q10, Q11, Q12, Q13, Q14, Q15, Q16, Q17, Q18, Q19, Q20, Q21, Q22, Q23, Q24, Q25, Q26, Q27, Q28, Q29, Q30, Q31, Q32, Q33, Q34, Q35]), "radius" : 2.5 * mm, "tangentPropagation" : true, "allowEdgeOverflow" : false});
        }
        {
            var Q0;
            Q0=makeQuery(id+"F1.opExtrude","SWEPT_EDGE",EDGE,{"disambiguationData":[OSD([sQuery(id+"F0.wireOp",EDGE,"E10.bottom"),sQuery(id+"F0.wireOp",EDGE,"E10.left")])]});
            var Q1;
            Q1=makeQuery(id+"F1.opExtrude","SWEPT_EDGE",EDGE,{"disambiguationData":[OSD([sQuery(id+"F0.wireOp",EDGE,"E10.bottom"),sQuery(id+"F0.wireOp",EDGE,"E10.right")])]});
            var Q2;
            Q2=makeQuery(id+"F1.opExtrude","SWEPT_EDGE",EDGE,{"disambiguationData":[OSD([sQuery(id+"F0.wireOp",EDGE,"E10.top"),sQuery(id+"F0.wireOp",EDGE,"E10.left")])]});
            var Q3;
            Q3=makeQuery(id+"F1.opExtrude","SWEPT_EDGE",EDGE,{"disambiguationData":[OSD([sQuery(id+"F0.wireOp",EDGE,"E10.top"),sQuery(id+"F0.wireOp",EDGE,"E10.right")])]});
            fillet(context, id + "F4", {"entities" : qUnion([Q0, Q1, Q2, Q3]), "radius" : 5 * mm, "allowEdgeOverflow" : false});
        }
        {
            var Q0;
            Q0=makeQuery(id+"F1.opExtrude","SWEPT_EDGE",EDGE,{"disambiguationData":[OSD([sQuery(id+"F0.wireOp",EDGE,"E6.rect.top"),sQuery(id+"F0.wireOp",EDGE,"E6.rect.left")])]});
            var Q1;
            Q1=makeQuery(id+"F1.opExtrude","SWEPT_EDGE",EDGE,{"disambiguationData":[OSD([sQuery(id+"F0.wireOp",EDGE,"E6.rect.bottom"),sQuery(id+"F0.wireOp",EDGE,"E6.rect.left")])]});
            var Q2;
            Q2=makeQuery(id+"F1.opExtrude","SWEPT_EDGE",EDGE,{"disambiguationData":[OSD([sQuery(id+"F0.wireOp",EDGE,"E6.rect.top"),sQuery(id+"F0.wireOp",EDGE,"E6.rect.right")])]});
            var Q3;
            Q3=makeQuery(id+"F1.opExtrude","SWEPT_EDGE",EDGE,{"disambiguationData":[OSD([sQuery(id+"F0.wireOp",EDGE,"E6.rect.bottom"),sQuery(id+"F0.wireOp",EDGE,"E6.rect.right")])]});
            fillet(context, id + "F5", {"entities" : qUnion([Q0, Q1, Q2, Q3]), "radius" : 15 * mm, "tangentPropagation" : true, "allowEdgeOverflow" : false});
        }
    });
